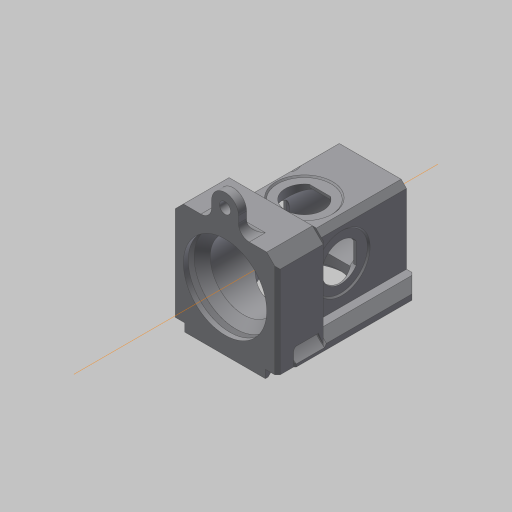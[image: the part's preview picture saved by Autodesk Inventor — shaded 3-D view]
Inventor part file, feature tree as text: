
AUTODESK INVENTOR PART (.ipt)
format: ipt  version: 2023.2 (Build 272271000, 271)  size: 838,656 bytes
history: native  units: mm
features: sketch x30, chamfer x19, hole x18, extrude x17, plane x14, other x10, fillet x5, projected_geometry x4, reference x3, emboss x1, revolve x1, pattern_circular x1, mirror x1
ambient origin geometry x8: Origin, YZ Plane, XZ Plane, XY Plane, X Axis, Y Axis, Z Axis, Center Point
bodies: Volumenkörper1 (feature_tree)
feature tree (124):
  extrude  "Extrusion1"  Depth=40.0mm
  extrude  "Extrusion2"  Depth=47.5mm TaperAngle=0.0deg
  extrude  "Extrusion3"  Depth=23.0mm
  extrude  "Extrusion4"  Depth=20.594885mm
  sketch  "Skizze2"  dims[d2=36.0mm d3=47.5mm d4=0.0mm]
  sketch  "Skizze3"  dims[d5=23.5mm d6=23.0mm]
  hole  "Bohrung2"  [1 undecoded]
  hole  "Bohrung1"  [1 undecoded]
  hole  "Bohrung9"  [1 undecoded]
  hole  "Bohrung3"  [1 undecoded]
  sketch  "Skizze4"  dims[d7=22.0mm d8=6.0mm d9=4.0mm d10=2.0mm d11=90.0deg d12=44.5mm d13=20.594885mm]
  hole  "Bohrung4"  [1 undecoded]
  hole  "Bohrung5"  [1 undecoded]
  hole  "Bohrung6"  [1 undecoded]
  hole  "Bohrung7"  [1 undecoded]
  hole  "Bohrung8"  [1 undecoded]
  hole  "Bohrung12"  [1 undecoded]
  hole  "Bohrung13"  [1 undecoded]
  hole  "Bohrung14"  [1 undecoded]
  chamfer  "Fase1"  Distance=13.0mm
  chamfer  "Fase2"  Distance=3.0mm Angle=45.0deg
  chamfer  "Fase3"  Distance=4.5mm
  chamfer  "Fase4"  Distance=16.0mm
  chamfer  "Fase5"  Distance=4.0mm
  chamfer  "Fase6"  Distance=4.0mm
  chamfer  "Fase7"  Distance=16.0mm
  chamfer  "Fase8"  Distance=16.0mm
  hole  "Bohrung15"  [1 undecoded]
  extrude  "Extrusion5"  Depth=1.0mm
  extrude  "Extrusion6"  Depth=1.0mm
  plane  "Arbeitsebene2"
  plane  "Arbeitsebene4"
  hole  "Bohrung17"  [1 undecoded]
  plane  "Work Plane6"
  plane  "Work Plane5"
  extrude  "Extrusion9"  Depth=1.0mm
  plane  "Work Plane10"
  plane  "Work Plane8"
  sketch  "Skizze16"  dims[d82=23.5mm d83=28.0mm]
  extrude  "Extrusion7"  Depth=1.0mm
  extrude  "Extrusion10"  Depth=1.0mm
  chamfer  "Chamfer10"  Distance=3.0mm
  emboss  "Emboss1"
  extrude  "Extrusion12"  Depth=1.0mm TaperAngle=45.0deg
  fillet  "Fillet2"  Radius=4.0mm
  plane  "Work Plane11"
  extrude  "Extrusion13"  Depth=1.0mm TaperAngle=45.0deg
  fillet  "Fillet3"  Radius=3.04mm
  fillet  "Rundung1"  Radius=4.0mm
  chamfer  "Chamfer18"  Distance=21.0mm
  revolve  "Revolution1"  [1 undecoded]
  chamfer  "Chamfer11"  Distance=2.5mm
  plane  "Work Plane12"
  extrude  "Extrusion14"  Depth=1.0mm
  chamfer  "Chamfer12"  [1 undecoded]
  chamfer  "Chamfer13"  Distance=46.0mm
  chamfer  "Chamfer14"  [1 undecoded]
  chamfer  "Chamfer15"  Distance=3.0mm
  chamfer  "Chamfer16"  Distance=15.5mm
  plane  "Work Plane13"
  plane  "Work Plane14"
  hole  "Hole19"  [1 undecoded]
  extrude  "Extrusion15"  Depth=1.0mm TaperAngle=0.0deg
  fillet  "Fillet4"  Radius=3.0mm
  fillet  "Fillet5"  [1 undecoded]
  extrude  "Extrusion16"  Depth=1.0mm
  chamfer  "Chamfer19"  Distance=7.0mm
  chamfer  "Chamfer20"  Distance=31.0mm Angle=75.0deg
  extrude  "Extrusion17"  Depth=1.0mm
  pattern_circular  "Circular Pattern1"  [2 undecoded]
  extrude  "Extrusion8"  Depth=1.0mm TaperAngle=0.0deg
  extrude  "Extrusion11"  Depth=1.0mm TaperAngle=45.0deg
  chamfer  "Chamfer9"  Distance=8.3mm
  hole  "Bohrung18"  [1 undecoded]
  hole  "Bohrung10"  [1 undecoded]
  hole  "Bohrung11"  [1 undecoded]
  plane  "Arbeitsebene1"
  mirror  "Spiegeln1"
  sketch  "Skizze1"  dims[d0=20.0mm d1=40.0mm]
  sketch  "Skizze5"  dims[d14=26.0mm d15=6.0mm d16=4.0mm d17=2.0mm d18=90.0deg d19=23.0mm d20=0.0mm]
  sketch  "Skizze6"  dims[d242=10.0mm d243=10.0mm d23=35.5mm d24=8.2mm d25=4.0mm d26=2.0mm d27=90.0deg d28=1.2mm d29=0.0mm d30=23.5mm]
  sketch  "Skizze7"  dims[d31=23.0mm]
  sketch  "Skizze8"  dims[d32=14.0mm d33=5.0mm d34=4.0mm d35=2.0mm d36=90.0deg d37=6.0mm d38=0.0mm]
  sketch  "Skizze9"  dims[d39=14.0mm d40=5.0mm d41=4.0mm d42=2.0mm d43=90.0deg d44=6.0mm d45=0.0mm]
  sketch  "Skizze10"  dims[d240=10.0mm d241=10.0mm d48=14.0mm d49=5.0mm d50=4.0mm d51=2.0mm d52=90.0deg d53=0.5mm d54=0.0mm d56=6.0mm]
  sketch  "Skizze11"  dims[d57=28.0mm d58=28.0mm]
  sketch  "Skizze12"  dims[d59=28.0mm d60=50.0mm d61=0.0mm]
  sketch  "Skizze13"  dims[d62=10.0mm d63=10.0mm d64=14.0mm d65=5.0mm d66=4.0mm d67=2.0mm d68=90.0deg d69=6.0mm d70=0.0mm d71=4.0mm d72=2.0mm d73=45.0deg]
  plane  "Arbeitsebene3"
  other  "Arbeitsachse1"
  sketch  "Skizze15"  dims[d74=0.5mm d75=2.0mm d76=45.0deg d77=3.0mm d78=2.0mm d79=45.0deg]
  sketch  "Sketch18"  dims[d84=32.0mm d85=10.0mm d86=0.0mm]
  other  "Work Axis2"
  plane  "Work Plane7"
  projected_geometry  "Projected Loop1"
  other  "Work Axis3"
  plane  "Work Plane9"
  other  "Work Axis4"
  sketch  "Sketch19"  dims[d87=20.0mm d88=20.0mm]
  sketch  "Sketch20"  dims[d89=2.013mm d90=3.0mm d91=4.0mm d92=2.0mm d93=90.0deg d94=3.0mm d95=0.0mm d96=2.0mm d97=2.0mm d98=45.0deg]
  sketch  "Sketch21"  dims[d101=25.0mm d102=8.5mm d103=4.0mm d104=2.0mm d105=90.0deg d106=45.5mm d107=0.0mm]
  sketch  "Sketch22"  dims[d108=39.0mm d109=38.0mm d110=13.0mm d111=0.0mm d112=3.0mm d113=2.0mm d114=45.0deg]
  projected_geometry  "Projected Loop5"
  sketch  "Sketch23"  dims[d115=22.0mm]
  sketch  "Sketch24"  dims[d116=22.0mm]
  sketch  "Sketch25"  dims[d117=5.0mm d118=6.0mm d119=4.0mm d120=2.0mm d121=90.0deg d122=30.0mm d123=20.594885mm]
  sketch  "Sketch26"  dims[d124=4.0mm]
  sketch  "Sketch27"  dims[d125=16.0mm]
  reference  "Reference2"
  reference  "Reference3"
  other  "Work Axis5"
  sketch  "Sketch28"  dims[d126=23.0mm]
  projected_geometry  "Projected Loop9"
  sketch  "Sketch29"  dims[d127=13.2mm d128=4.5mm d129=0.0mm]
  projected_geometry  "Projected Loop11"
  sketch  "Sketch30"  dims[d130=13.2mm]
  sketch  "Sketch31"  dims[d131=13.2mm]
  reference  "Reference5"
  sketch  "Sketch32"  dims[d132=13.2mm d133=16.0mm d134=4.0mm d135=4.0mm d136=16.0mm d137=16.0mm d138=4.0mm d139=24.0mm d140=24.0mm d141=2.0mm d142=6.0mm d143=4.0mm d144=2.0mm d145=90.0deg d146=30.0mm d147=20.594885mm d148=25.4mm d149=25.4mm d150=27.4mm d151=27.4mm d152=3.0mm d153=0.0mm d154=4.0mm d155=2.0mm d156=45.0deg d157=4.0mm d158=2.0mm d159=45.0deg d160=2.0mm d161=2.0mm d162=45.0deg d190=10.0mm d191=10.0mm d165=19.9mm d166=6.0mm d167=4.0mm d168=2.0mm d169=90.0deg d170=0.5mm d171=0.0mm d172=10.0mm d173=10.0mm d174=19.9mm d175=6.0mm d176=4.0mm d177=2.0mm d178=90.0deg d179=0.5mm d180=0.0mm d181=10.0mm d182=10.0mm d183=19.9mm d184=6.0mm d185=4.0mm d186=2.0mm d187=90.0deg d188=0.5mm d189=0.0mm d192=3.04mm d193=4.0mm d194=21.0mm d195=4.134mm d196=7.0mm d197=4.0mm d198=2.0mm d199=90.0deg d200=8.0mm d201=0.0mm d202=23.0mm d203=2.5mm d204=3.5mm d217=-23.0mm d218=46.0mm d219=-7.853982mm d220=3.0mm d221=3.0mm d222=7.0mm d223=4.0mm d224=2.0mm d225=90.0deg d226=16.0mm d227=0.0mm d229=15.5mm d230=0.0mm d259=10.0mm d260=10.0mm d233=4.0mm d234=6.0mm d235=4.0mm d236=2.0mm d237=90.0deg d238=6.0mm d239=0.0mm d246=7.0mm d247=0.0mm d254=20.0mm d255=0.0mm d256=3.0mm d261=-5.235988mm d262=2.5mm d263=7.0mm d264=75.0deg d265=31.0mm d267=3.0mm d269=4.5mm d270=9.5mm d271=0.0mm d272=3.0mm d273=2.0mm d274=45.0deg d276=8.3mm d277=0.0mm d278=19.0mm d280=18.0mm d281=-3.839724mm d282=-7.853982mm d283=40.0mm d293=360.0deg d294=2.0mm d295=2.0mm d296=45.0deg d297=0.3mm d298=0.0mm d299=6.0mm d300=0.0mm d301=4.0mm d302=0.0mm d303=2.0mm d305=-6.0mm d306=1.0mm d308=5.5mm d311=11.0mm d312=0.0mm d316=9.5mm d321=0.0mm d322=31.0mm d323=2.171252mm d324=0.845184mm d325=2.0mm d327=1.5mm d328=1.5mm d329=1.5mm d330=1.5mm d331=3.0mm d332=2.0mm d333=45.0deg d334=1.0mm d335=2.5mm d336=0.5mm d337=0.0mm d340=1.5mm d341=3.5mm d342=3.5mm d343=0.0mm d344=1.0mm d345=2.0mm d346=45.0deg d347=1.0mm d348=2.0mm d349=30.0deg d350=1.0mm d351=2.0mm d352=30.0deg d353=1.0mm d354=2.0mm d355=30.0deg d356=22.0mm d357=135.0deg d358=1.2mm d359=6.0mm d360=3.0mm d361=2.0mm d362=30.0deg d366=3.0mm d367=6.0mm d368=5.0mm d369=14.0mm d370=90.0deg d371=20.0mm d372=20.594885mm d375=15.0mm d376=10.0mm d378=1.0mm d379=4.610594mm d380=0.7mm d381=2.0mm d382=45.0deg d383=6.5mm d384=10.0mm d385=4.1mm d386=3.0mm d387=0.0mm d388=4.0mm d389=3.0mm d390=30.0mm d391=4.0mm d392=0.0mm d393=3.0mm d394=2.0mm d395=45.0deg d396=3.0mm d397=11.5mm d398=45.0deg d399=0.5mm d400=2.0mm d401=45.0deg d402=1.2mm d403=1.0mm d404=0.0mm d405=30.0mm d406=180.0deg d408=9.765513mm d80=1.0mm d81=1.0mm d206=1.0mm d207=1.0mm d228=1.0mm d258=1.0mm d284=1.0mm d285=1.0mm d286=0.15mm d287=0.25mm d288=0.375mm d289=14.3117mm d290=0.75mm d291=20.594885mm d292=0.0625mm d304=0.75mm d307=0.5mm d317=0.5mm d318=0.872665mm d319=0.5mm d320=0.872665mm d326=0.872665mm d338=0.0mm d339=0.0mm d374=1.0mm d377=0.15mm d409=1.0mm d410=1.0mm d411=1.0mm d412=0.15mm d413=3.0mm d414=5.0mm d415=14.3117mm d416=0.75mm d417=20.594885mm d418=0.0625mm d419=0.75mm d420=0.375mm]
  parser-record x1  (decoder bookkeeping rows leaked as tree rows — omitted from the tree; the rows remain in map.json)
  other  "chamber_assembly_3Dprint.iam"
  other  "rod_seal_friction:1"
  other  "Sealingring_holder:1"
  other  "chamber bottom seal plate:1"
note: 24 required parameter values undecoded (feature->parameter linkage not recoverable at this tier; creation-order binding heuristic only, values carry confidence <= 0.55)
note: 1 file-system path scrubbed to <path> (originals preserved in map.json)